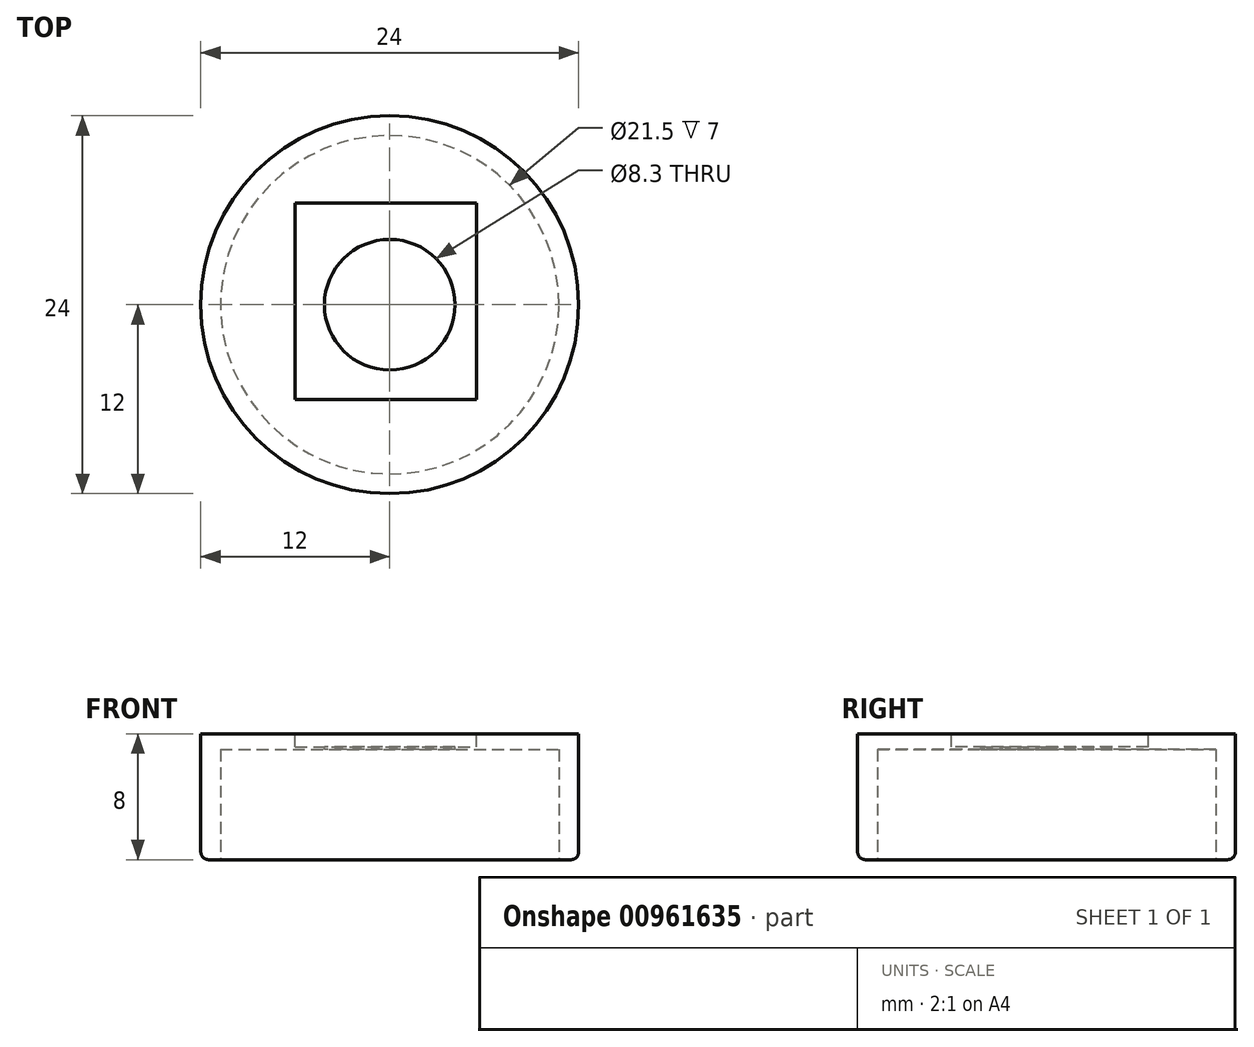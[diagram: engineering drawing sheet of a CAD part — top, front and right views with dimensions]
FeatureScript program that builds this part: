
annotation { "Feature Type Name" : "Feature", "Feature Type Description" : "" }
export const myFeature = defineFeature(function(context is Context, id is Id, definition is map)
    precondition{}
    {
        {
            var Q0;
            Q0=qCreatedBy(makeId("Top.planeOp"),FACE);
            var sketch = newSketch(context, id + "F0", { "sketchPlane" : qUnion([Q0])});
            skCircle(sketch, "E0", {"center": v(0, 0) * mm, "radius": 12 * mm});
            skSolve(sketch);
        }
        {
            var Q0;
            Q0=qSketchRegion(id+"F0",true);
            extrude(context, id + "F1", {"entities" : qUnion([Q0]), "depth" : 8 * mm, "offsetDistance" : 25 * mm});
        }
        {
            var Q0;
            Q0=makeQuery(id+"F1.opExtrude","CAP_FACE",FACE,{"disambiguationData":[OSD([sQuery(id+"F0.wireOp",EDGE,"E0")])],"isStart":true});
            var sketch = newSketch(context, id + "F2", { "sketchPlane" : qUnion([Q0])});
            skCircle(sketch, "E1", {"center": v(0, 0) * mm, "radius": 10.75 * mm});
            skSolve(sketch);
        }
        {
            var Q0;
            Q0=makeQuery(id+"F2.imprint","IMPRINT",FACE,{"disambiguationData":[TD([[makeQuery(id+"F2.imprint","IMPRINT",EDGE,{"derivedFrom":sQuery(id+"F2.wireOp",EDGE,"E1")}),1.0]])]});
            extrude(context, id + "F3", {"entities" : qUnion([Q0]), "operationType" : NewBodyOperationType.REMOVE, "oppositeDirection" : true, "depth" : 7 * mm, "offsetDistance" : 25 * mm});
        }
        {
            var Q0;
            Q0=makeQuery(id+"F1.opExtrude","CAP_FACE",FACE,{"disambiguationData":[OSD([sQuery(id+"F0.wireOp",EDGE,"E0")])],"isStart":false});
            var sketch = newSketch(context, id + "F4", { "sketchPlane" : qUnion([Q0])});
            skLineSegment(sketch, "E2.bottom", {"start": v(-6, 6.47) * mm, "end": v(5.5, 6.47) * mm});
            skLineSegment(sketch, "E2.top", {"start": v(-6, -6.03) * mm, "end": v(5.5, -6.03) * mm});
            skLineSegment(sketch, "E2.left", {"start": v(-6, 6.47) * mm, "end": v(-6, -6.03) * mm});
            skLineSegment(sketch, "E2.right", {"start": v(5.5, 6.47) * mm, "end": v(5.5, -6.03) * mm});
            skSolve(sketch);
        }
        {
            var Q0;
            Q0=makeQuery(id+"F4.imprint","IMPRINT",FACE,{"disambiguationData":[TD([[makeQuery(id+"F4.imprint","IMPRINT",EDGE,{"derivedFrom":sQuery(id+"F4.wireOp",EDGE,"E2.bottom")}),-1.0]])]});
            extrude(context, id + "F5", {"entities" : qUnion([Q0]), "operationType" : NewBodyOperationType.REMOVE, "oppositeDirection" : true, "depth" : 0.85 * mm, "offsetDistance" : 25 * mm});
        }
        {
            var Q0;
            Q0=makeQuery(id+"F5.boolean.opBoolean","COPY",FACE,{"derivedFrom":makeQuery(id+"F5.opExtrude","CAP_FACE",FACE,{"disambiguationData":[OSD([sQuery(id+"F4.wireOp",EDGE,"E2.bottom"),sQuery(id+"F4.wireOp",EDGE,"E2.top"),sQuery(id+"F4.wireOp",EDGE,"E2.left"),sQuery(id+"F4.wireOp",EDGE,"E2.right")])],"isStart":false})});
            var sketch = newSketch(context, id + "F6", { "sketchPlane" : qUnion([Q0])});
            skCircle(sketch, "E3", {"center": v(0, 0) * mm, "radius": 4.15 * mm});
            skSolve(sketch);
        }
        {
            var Q0;
            Q0 = qSketchRegion(id + "F6", true);
            extrude(context, id + "F7", {"entities" : qUnion([Q0]), "operationType" : NewBodyOperationType.REMOVE, "oppositeDirection" : true, "depth" : 0.15 * mm, "offsetDistance" : 25 * mm});
        }
        {
            var Q0;
            Q0=makeQuery(id+"F1.opExtrude","CAP_EDGE",EDGE,{"disambiguationData":[OSD([sQuery(id+"F0.wireOp",EDGE,"E0")])],"isStart":true});
            var Q1;
            Q1=makeQuery(id+"F3.boolean.opBoolean","COPY",EDGE,{"derivedFrom":makeQuery(id+"F3.opExtrude","CAP_EDGE",EDGE,{"disambiguationData":[OSD([sQuery(id+"F2.wireOp",EDGE,"E1")])],"isStart":true})});
            fillet(context, id + "F8", {"entities" : qUnion([Q0, Q1]), "radius" : 0.5 * mm, "tangentPropagation" : true, "allowEdgeOverflow" : false});
        }
    });
